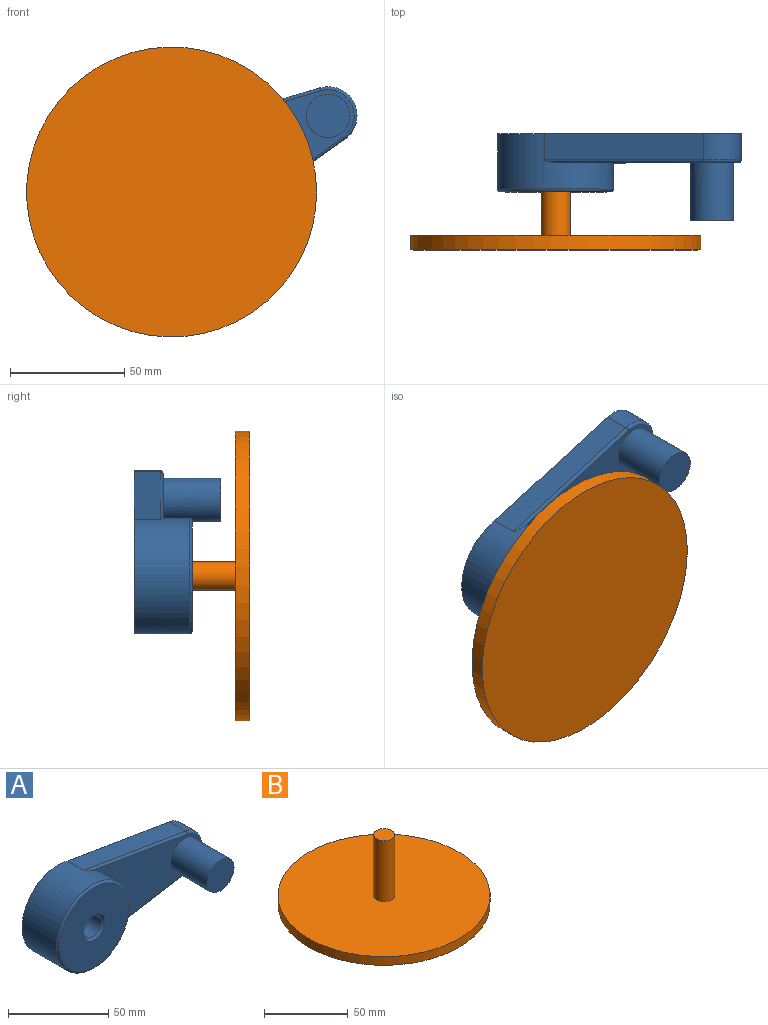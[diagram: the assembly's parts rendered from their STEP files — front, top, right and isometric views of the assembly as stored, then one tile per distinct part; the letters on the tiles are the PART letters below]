
ASSEMBLY  parts=2 mates=1
PART A: 15 faces, bbox 117.4x38.1x55 mm
  f0: plane 75.55x44.68mm, normal (0,-1,0), area 1672.3mm2, adj f1,f8,f9,f10,f13
  f1: cylinder r=25.4mm len=50.8mm, axis (0,1,0), area 3006mm2, adj f0,f2,f4,f6,f8,f10,f11
  f2: plane 71.92x12.06mm, normal (0.17,0,-0.99), area 833.5mm2, adj f1,f3,f6,f8
  f3: cylinder r=12.7mm len=25.05mm, axis (0,1,0), area 407.8mm2, adj f2,f4,f6,f9
  f4: plane 71.92x12.06mm, normal (0.17,0,0.99), area 833.5mm2, adj f1,f3,f6,f10
  f5: cylinder r=6.35mm len=24.13mm, axis (0,1,0), area 962.7mm2, adj f6,f12
  f6: plane 114.3x50.8mm, normal (0,1,0), area 4076.7mm2, adj f1,f2,f3,f4,f5
  f7: plane 48.26x48.26mm, normal (0,-1,0), area 1646.8mm2, adj f11,f12
  f8: cylinder r=1.27mm len=72.13mm, axis (-0.99,0,-0.17), area 140.1mm2, adj f0,f1,f2,f9
  f9: torus R=11.43mm, axis (0,-1,0), area 68.6mm2, adj f0,f3,f8,f10
  f10: cylinder r=1.27mm len=72.13mm, axis (0.99,0,-0.17), area 140.1mm2, adj f0,f1,f4,f9
  f11: torus R=24.13mm, axis (0,-1,0), area 312.6mm2, adj f1,f7
  f12: cone r=6.35mm half-angle=45deg, axis (0,-1,0), area 78.8mm2, adj f5,f7
  f13: cylinder r=9.53mm len=25.4mm, axis (0,1,0), area 1520.1mm2, adj f0,f14
  f14: plane 19.05x19.05mm, normal (0,-1,0), area 285mm2, adj f13
PART B: 5 faces, bbox 127x127x50.8 mm
  f0: cylinder r=63.5mm len=127mm, axis (0,0,-1), area 2533.5mm2, adj f1,f2
  f1: plane 127x127mm, normal (0,0,1), area 12541mm2, adj f0,f3
  f2: plane 127x127mm, normal (0,0,-1), area 12667.7mm2, adj f0
  f3: cylinder r=6.35mm len=44.45mm, axis (0,0,-1), area 1773.5mm2, adj f1,f4
  f4: plane 12.7x12.7mm, normal (0,0,1), area 126.7mm2, adj f3
PLACE A rot(axis=(0,-1,0),26deg) t=(-17.52,-15.77,-8.49)mm
PLACE B rot(axis=(-1,0,0),90deg) t=(-17.52,-66.57,-8.49)mm fixed
MATE revolute B.f3 <-> A.f1  axis (0,-1,0) through (-17.52,-15.77,-8.49)mm
